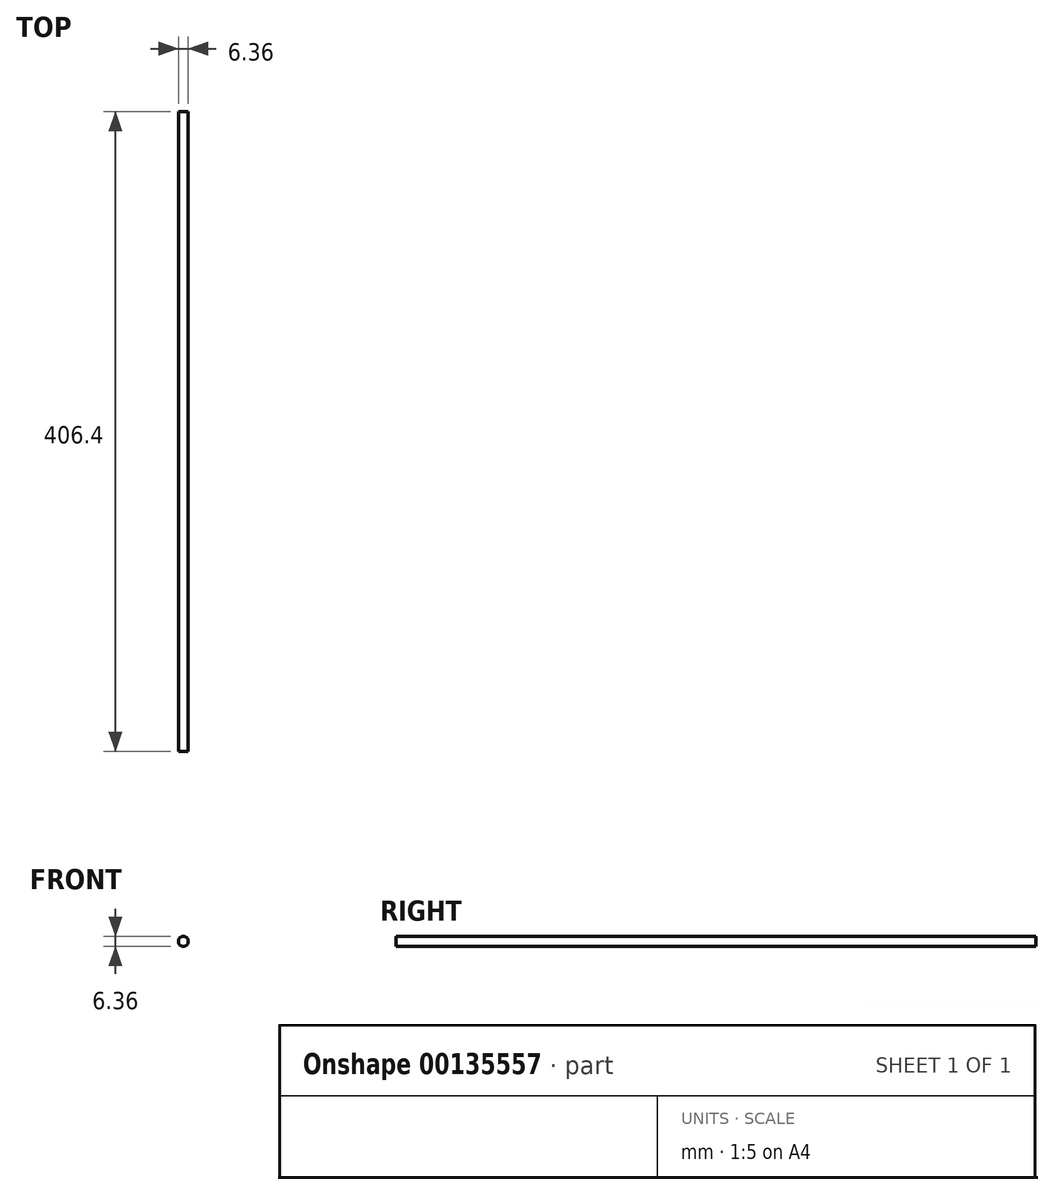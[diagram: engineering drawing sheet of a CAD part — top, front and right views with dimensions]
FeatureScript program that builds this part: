
annotation { "Feature Type Name" : "Feature", "Feature Type Description" : "" }
export const myFeature = defineFeature(function(context is Context, id is Id, definition is map)
    precondition{}
    {
        {
            var Q0;
            Q0=qCreatedBy(makeId("Front.planeOp"),FACE);
            var sketch = newSketch(context, id + "F0", { "sketchPlane" : qUnion([Q0])});
            skCircle(sketch, "E0", {"center": v(0, 0) * mm, "radius": 3.18 * mm});
            skSolve(sketch);
        }
        {
            var Q0;
            Q0=sQuery(id+"F0.wireOp",EDGE,"E0");
            extrude(context, id + "F1", {"bodyType" : ToolBodyType.SURFACE, "surfaceEntities" : qUnion([Q0]), "endBound" : BoundingType.SYMMETRIC, "depth" : 406.4 * mm});
        }
    });
